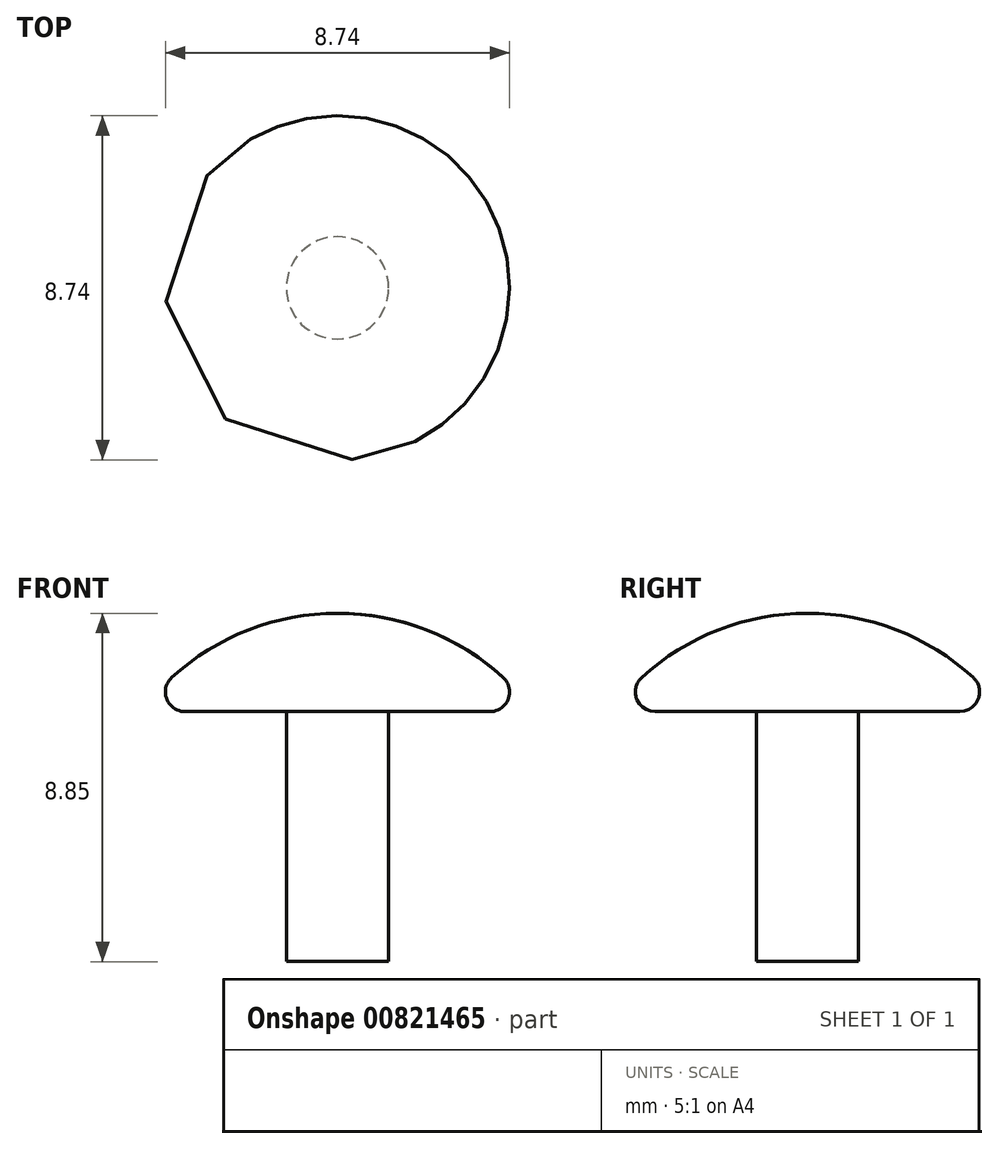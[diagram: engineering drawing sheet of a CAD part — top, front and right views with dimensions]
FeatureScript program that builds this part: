
annotation { "Feature Type Name" : "Feature", "Feature Type Description" : "" }
export const myFeature = defineFeature(function(context is Context, id is Id, definition is map)
    precondition{}
    {
        {
            var Q0;
            Q0=qCreatedBy(makeId("Front.planeOp"),FACE);
            var sketch = newSketch(context, id + "F0", { "sketchPlane" : qUnion([Q0])});
            skLineSegment(sketch, "E0", {"start": v(-5.05, -0.95) * mm, "end": v(4.95, -0.95) * mm});
            skArc(sketch, "E1", {"start": v(4.95, -0.95) * mm, "mid": v(-0.05, 1.55) * mm, "end": v(-5.05, -0.95) * mm});
            skLineSegment(sketch, "E2.bottom", {"start": v(-0.05, -0.95) * mm, "end": v(1.25, -0.95) * mm});
            skLineSegment(sketch, "E2.top", {"start": v(-0.05, -7.3) * mm, "end": v(1.25, -7.3) * mm});
            skLineSegment(sketch, "E2.left", {"start": v(-0.05, -0.95) * mm, "end": v(-0.05, -7.3) * mm});
            skLineSegment(sketch, "E2.right", {"start": v(1.25, -0.95) * mm, "end": v(1.25, -7.3) * mm});
            skLineSegment(sketch, "E3", {"start": v(-0.05, -0.95) * mm, "end": v(-0.05, 1.55) * mm});
            skSolve(sketch);
        }
        {
            var Q0;
            {var subQ4=sQuery(id+"F0.wireOp",EDGE,"E3");Q0=makeQuery(id+"F0.imprint","IMPRINT",FACE,{"disambiguationData":[TD([[makeQuery(id+"F0.imprint","IMPRINT",EDGE,{"derivedFrom":subQ4}),-1.0]])]});}
            var Q1;
            Q1=makeQuery(id+"F0.imprint","IMPRINT",FACE,{"disambiguationData":[TD([[makeQuery(id+"F0.imprint","IMPRINT",EDGE,{"derivedFrom":sQuery(id+"F0.wireOp",EDGE,"E2.top")}),1.0]])]});
            var Q2;
            Q2=sQuery(id+"F0.wireOp",EDGE,"E2.left");
            revolve(context, id + "F1", {"surfaceOperationType" : NewSurfaceOperationType.NEW, "entities" : qUnion([Q0, Q1]), "axis" : qUnion([Q2]), "revolveType" : RevolveType.FULL});
        }
        {
            var Q0;
            Q0=makeQuery(id+"F1.opRevolve","SWEPT_EDGE",EDGE,{"disambiguationData":[OSD([sQuery(id+"F0.wireOp",EDGE,"E0"),sQuery(id+"F0.wireOp",EDGE,"E1")])]});
            fillet(context, id + "F2", {"entities" : qUnion([Q0]), "radius" : 0.5 * mm, "tangentPropagation" : true, "allowEdgeOverflow" : false});
        }
    });
